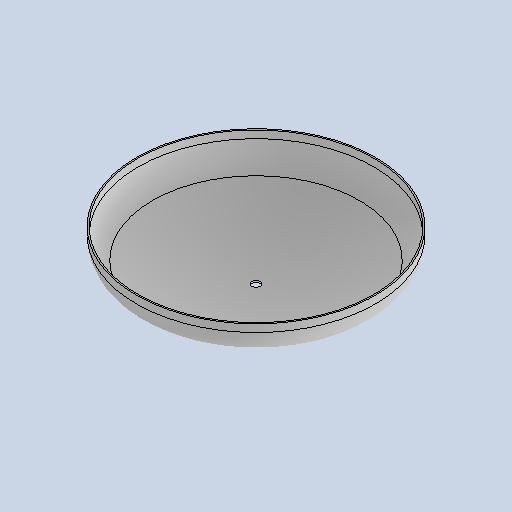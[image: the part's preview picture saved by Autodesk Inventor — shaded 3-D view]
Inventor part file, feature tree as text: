
AUTODESK INVENTOR PART (.ipt)
format: ipt  version: 2025.1 (Build 291241020, 241B)  size: 161,792 bytes
history: native  units: mm
features: sketch x2, revolve x1, extrude x1
ambient origin geometry x8: Origin, YZ Plane, XZ Plane, XY Plane, X Axis, Y Axis, Z Axis, Center Point
bodies: Solid1 (feature_tree)
feature tree (4):
  revolve  "Revolution1"  [1 undecoded]
  extrude  "Extrusion1"  Depth=1080.006667mm
  sketch  "Sketch1"  dims[d0=100.0mm d1=30.0mm]
  sketch  "Sketch2"  dims[d3=1080.006667mm d6=6.0mm d7=90.0deg d8=33.5mm d9=0.0mm d10=0.0mm d11=940.0mm d12=205.0mm]
note: 1 required parameter value undecoded (feature->parameter linkage not recoverable at this tier; creation-order binding heuristic only, values carry confidence <= 0.55)
